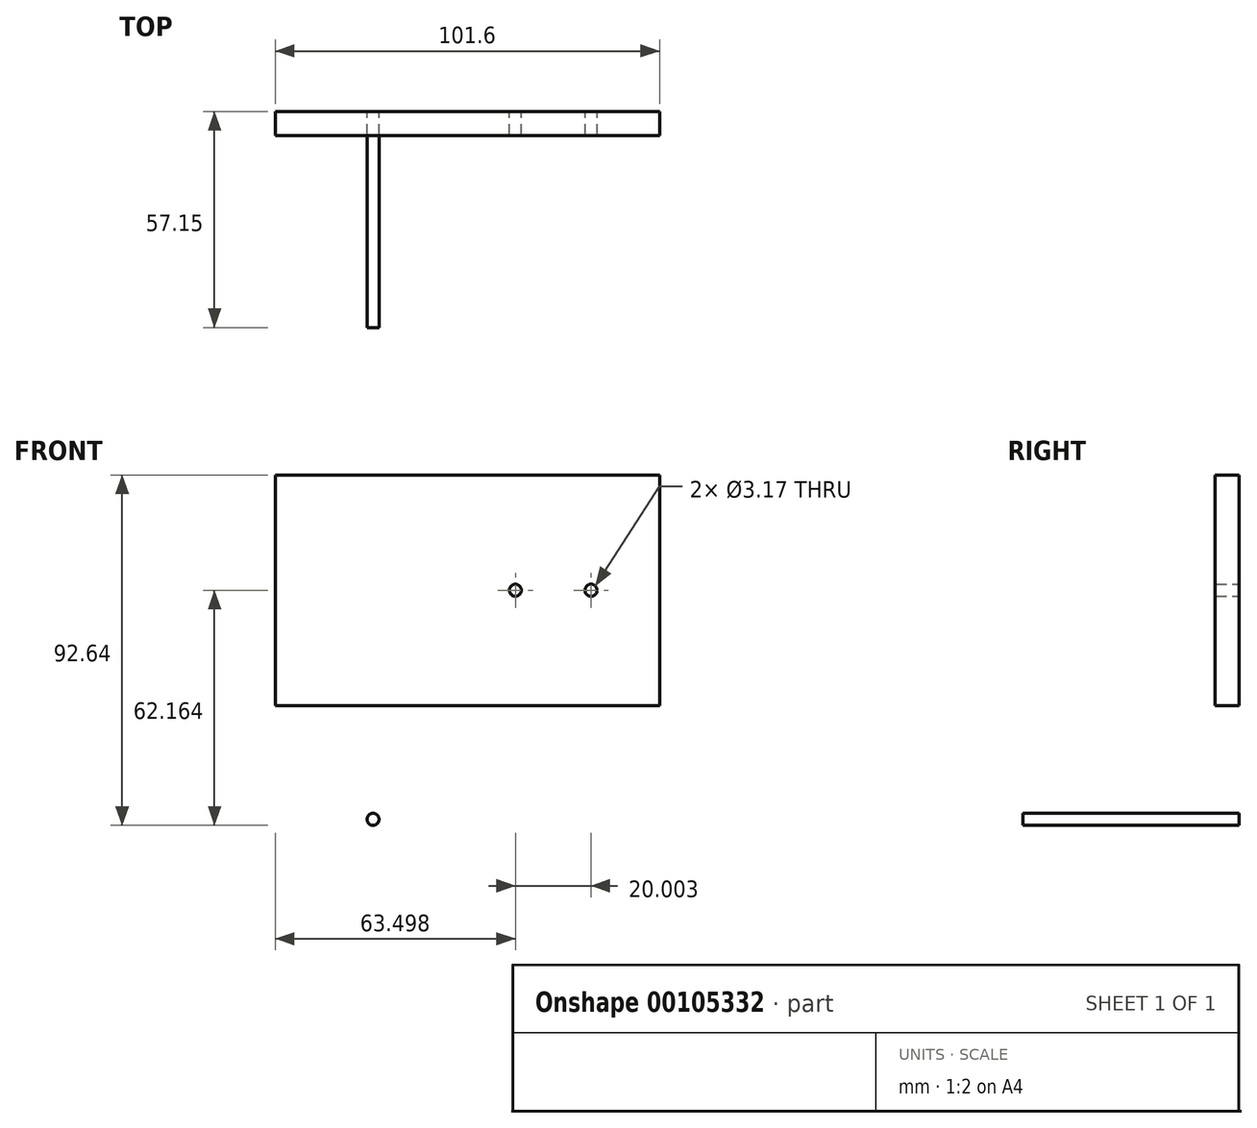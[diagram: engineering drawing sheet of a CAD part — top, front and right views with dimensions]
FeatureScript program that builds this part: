
annotation { "Feature Type Name" : "Feature", "Feature Type Description" : "" }
export const myFeature = defineFeature(function(context is Context, id is Id, definition is map)
    precondition{}
    {
        {
            var Q0;
            Q0=qCreatedBy(makeId("Front.planeOp"),FACE);
            var sketch = newSketch(context, id + "F0", { "sketchPlane" : qUnion([Q0])});
            skLineSegment(sketch, "E0.bottom", {"start": v(-83.5, 78.07) * mm, "end": v(18.1, 78.07) * mm});
            skLineSegment(sketch, "E0.top", {"start": v(-83.5, 17.11) * mm, "end": v(18.1, 17.11) * mm});
            skLineSegment(sketch, "E0.left", {"start": v(-83.5, 78.07) * mm, "end": v(-83.5, 17.11) * mm});
            skLineSegment(sketch, "E0.right", {"start": v(18.1, 78.07) * mm, "end": v(18.1, 17.11) * mm});
            skCircle(sketch, "E1", {"center": v(-57.63, -12.98) * mm, "radius": 1.59 * mm});
            skCircle(sketch, "E2", {"center": v(-20, 47.6) * mm, "radius": 1.59 * mm});
            skPoint(sketch, "E2.centerSnap0", {"position": v(-83.5, 47.6) * mm});
            skPoint(sketch, "E3", {"position": v(0, 47.6) * mm});
            skPoint(sketch, "E3.positionSnap0", {"position": v(18.1, 47.6) * mm});
            skCircle(sketch, "E4", {"center": v(0, 47.6) * mm, "radius": 1.59 * mm});
            skSolve(sketch);
        }
        {
            var Q0;
            Q0 = qSketchRegion(id + "F0", true);
            extrude(context, id + "F1", {"entities" : qUnion([Q0]), "depth" : 6.35 * mm});
        }
        {
            var Q0;
            Q0=makeQuery(id+"F1.opExtrude","CAP_FACE",FACE,{"disambiguationData":[OSD([sQuery(id+"F0.wireOp",EDGE,"E1")])],"isStart":false});
            var Q1;
            Q1=makeQuery(id+"F1.opExtrude","CAP_FACE",FACE,{"disambiguationData":[OSD([sQuery(id+"F0.wireOp",EDGE,"E1")])],"isStart":true});
            extrude(context, id + "F2", {"entities" : qUnion([Q0, Q1]), "operationType" : NewBodyOperationType.ADD, "depth" : 50.8 * mm});
        }
    });
